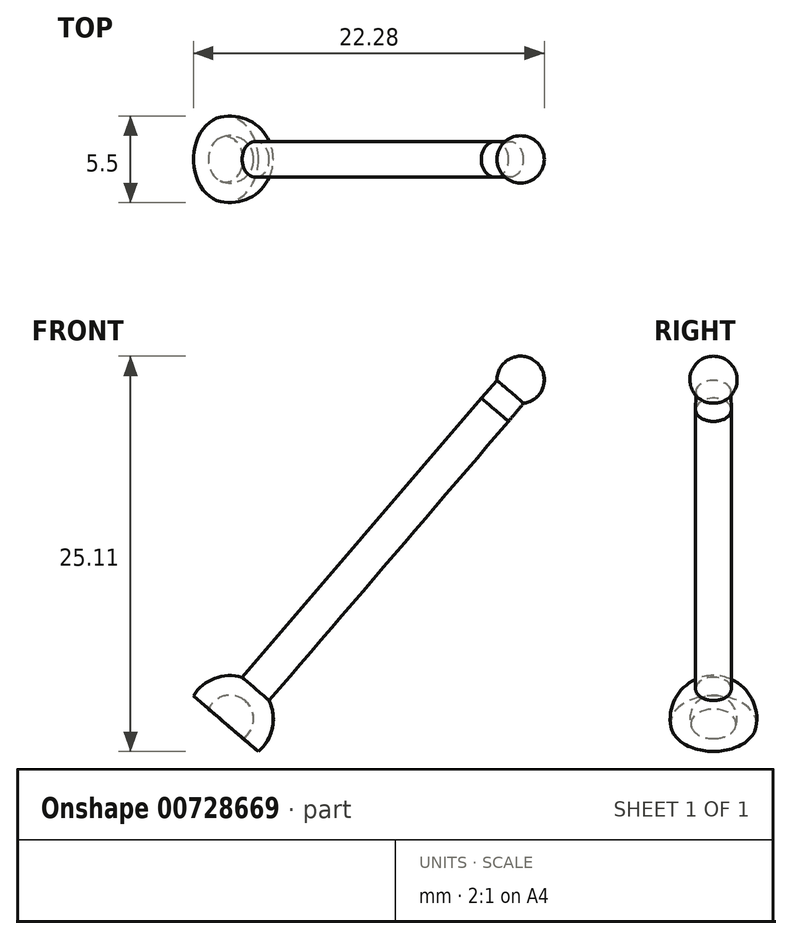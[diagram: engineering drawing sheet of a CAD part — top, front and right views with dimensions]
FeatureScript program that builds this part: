
annotation { "Feature Type Name" : "Feature", "Feature Type Description" : "" }
export const myFeature = defineFeature(function(context is Context, id is Id, definition is map)
    precondition{}
    {
        {
            var Q0;
            Q0=qCreatedBy(makeId("Front.planeOp"),FACE);
            var sketch = newSketch(context, id + "F0", { "sketchPlane" : qUnion([Q0])});
            skLineSegment(sketch, "E0", {"start": v(-12.74, -33.58) * mm, "end": v(-16.2, -77.78) * mm});
            skLineSegment(sketch, "E1", {"start": v(-33.18, -4.67) * mm, "end": v(-51.9, -21.6) * mm});
            skLineSegment(sketch, "E2", {"start": v(0, 33.27) * mm, "end": v(0, 17.24) * mm});
            skLineSegment(sketch, "E3", {"start": v(0, 17.24) * mm, "end": v(0, -22.87) * mm});
            skLineSegment(sketch, "E4", {"start": v(0, -22.87) * mm, "end": v(0, -36.97) * mm});
            skLineSegment(sketch, "E5", {"start": v(0, -36.97) * mm, "end": v(-12.74, -33.58) * mm});
            skLineSegment(sketch, "E6", {"start": v(-0.06, 17.24) * mm, "end": v(0, 17.24) * mm});
            skLineSegment(sketch, "E7", {"start": v(-16.2, -77.78) * mm, "end": v(-22.22, -118.07) * mm});
            skLineSegment(sketch, "E8.MirrorCS", {"start": v(16.2, -77.78) * mm, "end": v(22.22, -118.07) * mm});
            skLineSegment(sketch, "E9.MirrorCS", {"start": v(14.72, 16.87) * mm, "end": v(33.18, -4.67) * mm});
            skLineSegment(sketch, "E10.MirrorCS", {"start": v(33.18, -4.67) * mm, "end": v(51.9, -21.6) * mm});
            skLineSegment(sketch, "E11.MirrorCS", {"start": v(12.74, -33.58) * mm, "end": v(16.2, -77.78) * mm});
            skLineSegment(sketch, "E12.MirrorCS", {"start": v(0, -36.97) * mm, "end": v(12.74, -33.58) * mm});
            skLineSegment(sketch, "E13.MirrorCS", {"start": v(14.72, 16.87) * mm, "end": v(0, 17.24) * mm});
            skArc(sketch, "E14", {"start": v(-14.53, 15.38) * mm, "mid": v(-13.73, 18) * mm, "end": v(-16.22, 16.85) * mm});
            skCircle(sketch, "E15", {"center": v(-33.18, -4.67) * mm, "radius": 1.5 * mm});
            skCircle(sketch, "E16", {"center": v(-51.9, -21.6) * mm, "radius": 1.5 * mm});
            skCircle(sketch, "E17", {"center": v(-12.74, -33.58) * mm, "radius": 1.5 * mm});
            skCircle(sketch, "E18.MirrorC", {"center": v(33.18, -4.67) * mm, "radius": 1.5 * mm});
            skCircle(sketch, "E19.MirrorC", {"center": v(51.9, -21.6) * mm, "radius": 1.5 * mm});
            skCircle(sketch, "E20.MirrorC", {"center": v(14.72, 16.87) * mm, "radius": 1.5 * mm});
            skCircle(sketch, "E21.MirrorC", {"center": v(12.74, -33.58) * mm, "radius": 1.5 * mm});
            skArc(sketch, "E22", {"start": v(-15.49, 14.23) * mm, "mid": v(-13.77, 14.29) * mm, "end": v(-12.42, 15.36) * mm});
            skArc(sketch, "E23", {"start": v(-32.6, -1.98) * mm, "mid": v(-34.89, -6.82) * mm, "end": v(-30.69, -3.5) * mm});
            skLineSegment(sketch, "E24", {"start": v(-32.6, -1.98) * mm, "end": v(-17.21, 15.7) * mm});
            skLineSegment(sketch, "E25", {"start": v(-17.21, 15.7) * mm, "end": v(-16.22, 16.85) * mm});
            skLineSegment(sketch, "E26", {"start": v(-14.53, 15.38) * mm, "end": v(-15.49, 14.23) * mm});
            skLineSegment(sketch, "E27", {"start": v(-15.49, 14.23) * mm, "end": v(-30.69, -3.5) * mm});
            skLineSegment(sketch, "E28.trimOffspring", {"start": v(-16.5, 14.78) * mm, "end": v(-31.39, -2.58) * mm});
            skLineSegment(sketch, "E29.trimOffspring", {"start": v(-32.2, -3.53) * mm, "end": v(-33.18, -4.67) * mm});
            skLineSegment(sketch, "E30", {"start": v(-16.5, 14.78) * mm, "end": v(-13.74, 18) * mm});
            skLineSegment(sketch, "E31", {"start": v(-31.39, -2.58) * mm, "end": v(-32.2, -3.53) * mm});
            skLineSegment(sketch, "E32", {"start": v(-35.54, -3.27) * mm, "end": v(-31.37, -6.74) * mm});
            skLineSegment(sketch, "E33", {"start": v(-9.87, 19.09) * mm, "end": v(-9.84, 18.09) * mm});
            skLineSegment(sketch, "E34", {"start": v(-9.75, 14.43) * mm, "end": v(0, 14.67) * mm});
            skLineSegment(sketch, "E35", {"start": v(0, 14.67) * mm, "end": v(-0.11, 19.09) * mm});
            skLineSegment(sketch, "E36", {"start": v(-0.11, 19.09) * mm, "end": v(-9.87, 19.09) * mm});
            skLineSegment(sketch, "E37", {"start": v(-12.42, 15.36) * mm, "end": v(-3.46, 15.59) * mm});
            skLineSegment(sketch, "E38", {"start": v(-3.46, 15.59) * mm, "end": v(-3.46, 18.09) * mm});
            skLineSegment(sketch, "E39", {"start": v(-3.46, 18.09) * mm, "end": v(-12.25, 18.09) * mm});
            skArc(sketch, "E40.trimOffspring", {"start": v(-12.25, 18.09) * mm, "mid": v(-15.9, 19.35) * mm, "end": v(-17.21, 15.7) * mm});
            skLineSegment(sketch, "E41.trimOffspring", {"start": v(-9.77, 15.43) * mm, "end": v(-9.75, 14.43) * mm});
            skSolve(sketch);
        }
        {
            var Q0;
            {var subQ6=sQuery(id+"F0.wireOp",EDGE,"E26");Q0=makeQuery(id+"F0.imprint","IMPRINT",FACE,{"disambiguationData":[TD([[makeQuery(id+"F0.imprint","IMPRINT",EDGE,{"derivedFrom":subQ6}),-1.0]])]});}
            var Q1;
            Q1=sQuery(id+"F0.wireOp",EDGE,"E28.trimOffspring");
            revolve(context, id + "F1", {"surfaceOperationType" : NewSurfaceOperationType.NEW, "entities" : qUnion([Q0]), "axis" : qUnion([Q1]), "revolveType" : RevolveType.FULL});
        }
    });
